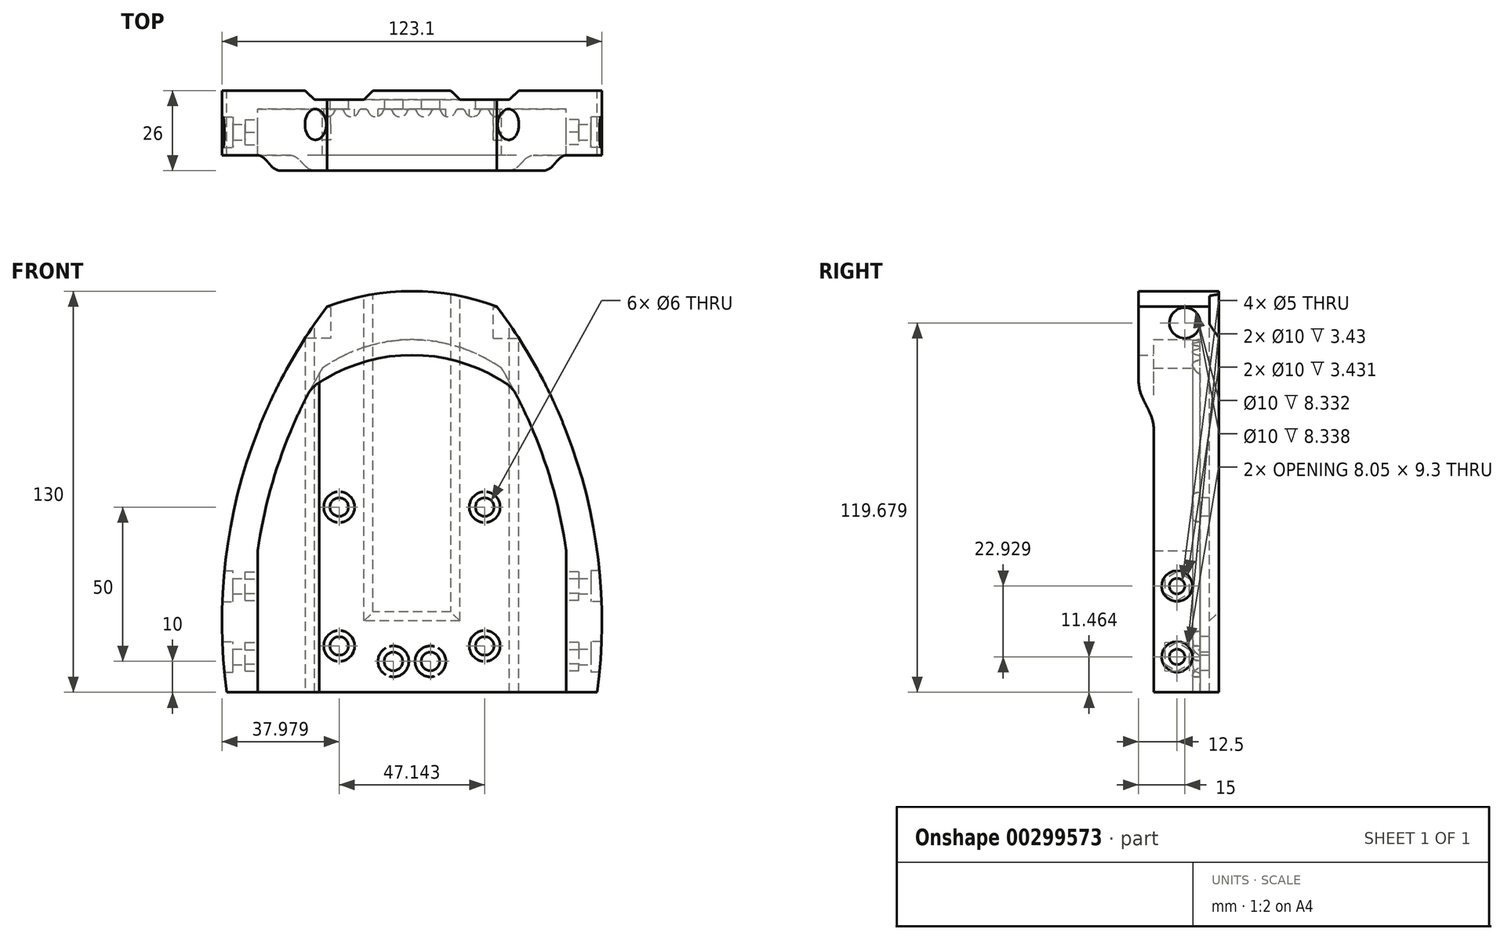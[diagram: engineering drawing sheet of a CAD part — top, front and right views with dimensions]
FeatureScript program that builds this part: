
annotation { "Feature Type Name" : "Feature", "Feature Type Description" : "" }
export const myFeature = defineFeature(function(context is Context, id is Id, definition is map)
    precondition{}
    {
        {
            assignVariable(context, id + "F0", {"name" : "TWall", "anyValue" : 10});
        }
        {
            var Q0;
            Q0=qCreatedBy(makeId("Front.planeOp"),FACE);
            var sketch = newSketch(context, id + "F1", { "sketchPlane" : qUnion([Q0])});
            skArc(sketch, "E0", {"start": v(-27.5, 125) * mm, "mid": v(-56.08, 65.7) * mm, "end": v(-60, 0) * mm});
            skArc(sketch, "E1", {"start": v(0, 130) * mm, "mid": v(-13.98, 128.74) * mm, "end": v(-27.5, 125) * mm});
            skLineSegment(sketch, "E2", {"start": v(-60, 0) * mm, "end": v(0, 0) * mm});
            skArc(sketch, "E3.MirrorCS", {"start": v(0, 130) * mm, "mid": v(13.98, 128.74) * mm, "end": v(27.5, 125) * mm});
            skArc(sketch, "E4.MirrorCS", {"start": v(27.5, 125) * mm, "mid": v(56.08, 65.7) * mm, "end": v(60, 0) * mm});
            skLineSegment(sketch, "E5.MirrorCS", {"start": v(60, 0) * mm, "end": v(0, 0) * mm});
            skSolve(sketch);
        }
        {
            var Q0;
            Q0 = qSketchRegion(id + "F1", true);
            extrude(context, id + "F2", {"entities" : qUnion([Q0]), "depth" : 3 * mm});
        }
        {
            var Q0;
            Q0=makeQuery(id+"F2.opExtrude","CAP_FACE",FACE,{"disambiguationData":[OSD([sQuery(id+"F1.wireOp",EDGE,"E0"),sQuery(id+"F1.wireOp",EDGE,"E1"),sQuery(id+"F1.wireOp",EDGE,"E2"),sQuery(id+"F1.wireOp",EDGE,"E3.MirrorCS"),sQuery(id+"F1.wireOp",EDGE,"E4.MirrorCS"),sQuery(id+"F1.wireOp",EDGE,"E5.MirrorCS")])],"isStart":false});
            var sketch = newSketch(context, id + "F3", { "sketchPlane" : qUnion([Q0])});
            skArc(sketch, "E6", {"start": v(27.5, 125) * mm, "mid": v(0, 130) * mm, "end": v(-27.5, 125) * mm});
            skArc(sketch, "E7", {"start": v(-27.5, 125) * mm, "mid": v(-56.08, 65.7) * mm, "end": v(-60, 0) * mm});
            skArc(sketch, "E8", {"start": v(60, 0) * mm, "mid": v(56.08, 65.7) * mm, "end": v(27.5, 125) * mm});
            skArc(sketch, "E9", {"start": v(29.01, 105) * mm, "mid": v(0, 114.28) * mm, "end": v(-29.01, 105) * mm});
            skArc(sketch, "E10", {"start": v(-29.01, 105) * mm, "mid": v(-48.55, 54.3) * mm, "end": v(-50, 0) * mm});
            skArc(sketch, "E11", {"start": v(50, 0) * mm, "mid": v(48.55, 54.3) * mm, "end": v(29.01, 105) * mm});
            skLineSegment(sketch, "E12", {"start": v(-60, 0) * mm, "end": v(-50, 0) * mm});
            skLineSegment(sketch, "E13", {"start": v(50, 0) * mm, "end": v(60, 0) * mm});
            skLineSegment(sketch, "E14", {"start": v(-50, 45.86) * mm, "end": v(-50, 0) * mm});
            skPoint(sketch, "E15", {"position": v(-50, 43.93) * mm});
            skLineSegment(sketch, "E16.MirrorCS", {"start": v(50, 45.86) * mm, "end": v(50, 0) * mm});
            skSolve(sketch);
        }
        {
            var Q0;
            Q0 = qSketchRegion(id + "F3", true);
            extrude(context, id + "F4", {"entities" : qUnion([Q0]), "operationType" : NewBodyOperationType.ADD, "depth" : 15 * mm});
        }
        {
            var Q0;
            Q0=makeQuery(id+"F2.opExtrude","SWEPT_FACE",FACE,{"disambiguationData":[OSD([sQuery(id+"F1.wireOp",EDGE,"E2"),sQuery(id+"F1.wireOp",EDGE,"E5.MirrorCS")])]});
            var sketch = newSketch(context, id + "F5", { "sketchPlane" : qUnion([Q0])});
            skArc(sketch, "E17", {"start": v(-25, 3) * mm, "mid": v(-27.5, 5.5) * mm, "end": v(-30, 3) * mm});
            skLineSegment(sketch, "E18", {"start": v(-30, 3) * mm, "end": v(-25, 3) * mm});
            skArc(sketch, "E19.1.0.0", {"start": v(-17.14, 3) * mm, "mid": v(-19.64, 5.5) * mm, "end": v(-22.14, 3) * mm});
            skLineSegment(sketch, "E19.1.0.1", {"start": v(-22.14, 3) * mm, "end": v(-17.14, 3) * mm});
            skArc(sketch, "E19.2.0.0", {"start": v(-9.29, 3) * mm, "mid": v(-11.79, 5.5) * mm, "end": v(-14.29, 3) * mm});
            skLineSegment(sketch, "E19.2.0.1", {"start": v(-14.29, 3) * mm, "end": v(-9.29, 3) * mm});
            skArc(sketch, "E19.3.0.0", {"start": v(-1.43, 3) * mm, "mid": v(-3.93, 5.5) * mm, "end": v(-6.43, 3) * mm});
            skLineSegment(sketch, "E19.3.0.1", {"start": v(-6.43, 3) * mm, "end": v(-1.43, 3) * mm});
            skArc(sketch, "E19.4.0.0", {"start": v(6.43, 3) * mm, "mid": v(3.93, 5.5) * mm, "end": v(1.43, 3) * mm});
            skLineSegment(sketch, "E19.4.0.1", {"start": v(1.43, 3) * mm, "end": v(6.43, 3) * mm});
            skArc(sketch, "E19.5.0.0", {"start": v(14.29, 3) * mm, "mid": v(11.79, 5.5) * mm, "end": v(9.29, 3) * mm});
            skLineSegment(sketch, "E19.5.0.1", {"start": v(9.29, 3) * mm, "end": v(14.29, 3) * mm});
            skArc(sketch, "E19.6.0.0", {"start": v(22.14, 3) * mm, "mid": v(19.64, 5.5) * mm, "end": v(17.14, 3) * mm});
            skLineSegment(sketch, "E19.6.0.1", {"start": v(17.14, 3) * mm, "end": v(22.14, 3) * mm});
            skArc(sketch, "E19.7.0.0", {"start": v(30, 3) * mm, "mid": v(27.5, 5.5) * mm, "end": v(25, 3) * mm});
            skLineSegment(sketch, "E19.7.0.1", {"start": v(25, 3) * mm, "end": v(30, 3) * mm});
            skLineSegment(sketch, "E19.direction1", {"start": v(-30, 3) * mm, "end": v(-22.14, 3) * mm, "construction": true});
            skSolve(sketch);
        }
        {
            var Q0;
            Q0 = qSketchRegion(id + "F5", true);
            extrude(context, id + "F6", {"entities" : qUnion([Q0]), "operationType" : NewBodyOperationType.ADD, "endBound" : BoundingType.UP_TO_NEXT, "oppositeDirection" : true, "depth" : 25 * mm});
        }
        {
            var Q0;
            {var subQ0=sQuery(id+"F5.wireOp",EDGE,"E18");var subQ1=sQuery(id+"F5.wireOp",EDGE,"E17");var subQ2=sQuery(id+"F1.wireOp",EDGE,"E5.MirrorCS");var subQ3=sQuery(id+"F1.wireOp",EDGE,"E2");Q0=makeQuery(id+"F6.opExtrude","SWEPT_EDGE",EDGE,{"disambiguationData":[OSD([subQ3,subQ2,subQ1,subQ0]),TDD([makeQuery(id+"F5.imprint","INTERSECT",VERTEX,{"disambiguationData":[OD(1.0)],"derivedFrom":[makeQuery(id+"F2.opExtrude","CAP_EDGE",EDGE,{"disambiguationData":[OSD([subQ3,subQ2])],"isStart":false}),subQ1,subQ0]})])]});}
            var Q1;
            {var subQ0=sQuery(id+"F5.wireOp",EDGE,"E18");var subQ1=sQuery(id+"F5.wireOp",EDGE,"E17");var subQ2=sQuery(id+"F1.wireOp",EDGE,"E5.MirrorCS");var subQ3=sQuery(id+"F1.wireOp",EDGE,"E2");Q1=makeQuery(id+"F6.opExtrude","SWEPT_EDGE",EDGE,{"disambiguationData":[OSD([subQ3,subQ2,subQ1,subQ0]),TDD([makeQuery(id+"F5.imprint","INTERSECT",VERTEX,{"disambiguationData":[OD(0.0)],"derivedFrom":[makeQuery(id+"F2.opExtrude","CAP_EDGE",EDGE,{"disambiguationData":[OSD([subQ3,subQ2])],"isStart":false}),subQ1,subQ0]})])]});}
            var Q2;
            {var subQ0=sQuery(id+"F5.wireOp",EDGE,"E19.1.0.1");var subQ1=sQuery(id+"F5.wireOp",EDGE,"E19.1.0.0");var subQ2=sQuery(id+"F1.wireOp",EDGE,"E5.MirrorCS");var subQ3=sQuery(id+"F1.wireOp",EDGE,"E2");Q2=makeQuery(id+"F6.opExtrude","SWEPT_EDGE",EDGE,{"disambiguationData":[OSD([subQ3,subQ2,subQ1,subQ0]),TDD([makeQuery(id+"F5.imprint","INTERSECT",VERTEX,{"disambiguationData":[OD(0.0)],"derivedFrom":[makeQuery(id+"F2.opExtrude","CAP_EDGE",EDGE,{"disambiguationData":[OSD([subQ3,subQ2])],"isStart":false}),subQ1,subQ0]})])]});}
            var Q3;
            {var subQ0=sQuery(id+"F5.wireOp",EDGE,"E19.2.0.1");var subQ1=sQuery(id+"F5.wireOp",EDGE,"E19.2.0.0");var subQ2=sQuery(id+"F1.wireOp",EDGE,"E5.MirrorCS");var subQ3=sQuery(id+"F1.wireOp",EDGE,"E2");Q3=makeQuery(id+"F6.opExtrude","SWEPT_EDGE",EDGE,{"disambiguationData":[OSD([subQ3,subQ2,subQ1,subQ0]),TDD([makeQuery(id+"F5.imprint","INTERSECT",VERTEX,{"disambiguationData":[OD(0.0)],"derivedFrom":[makeQuery(id+"F2.opExtrude","CAP_EDGE",EDGE,{"disambiguationData":[OSD([subQ3,subQ2])],"isStart":false}),subQ1,subQ0]})])]});}
            var Q4;
            {var subQ0=sQuery(id+"F5.wireOp",EDGE,"E19.3.0.1");var subQ1=sQuery(id+"F5.wireOp",EDGE,"E19.3.0.0");var subQ2=sQuery(id+"F1.wireOp",EDGE,"E5.MirrorCS");var subQ3=sQuery(id+"F1.wireOp",EDGE,"E2");Q4=makeQuery(id+"F6.opExtrude","SWEPT_EDGE",EDGE,{"disambiguationData":[OSD([subQ3,subQ2,subQ1,subQ0]),TDD([makeQuery(id+"F5.imprint","INTERSECT",VERTEX,{"disambiguationData":[OD(0.0)],"derivedFrom":[makeQuery(id+"F2.opExtrude","CAP_EDGE",EDGE,{"disambiguationData":[OSD([subQ3,subQ2])],"isStart":false}),subQ1,subQ0]})])]});}
            var Q5;
            {var subQ0=sQuery(id+"F5.wireOp",EDGE,"E19.4.0.1");var subQ1=sQuery(id+"F5.wireOp",EDGE,"E19.4.0.0");var subQ2=sQuery(id+"F1.wireOp",EDGE,"E5.MirrorCS");var subQ3=sQuery(id+"F1.wireOp",EDGE,"E2");Q5=makeQuery(id+"F6.opExtrude","SWEPT_EDGE",EDGE,{"disambiguationData":[OSD([subQ3,subQ2,subQ1,subQ0]),TDD([makeQuery(id+"F5.imprint","INTERSECT",VERTEX,{"disambiguationData":[OD(0.0)],"derivedFrom":[makeQuery(id+"F2.opExtrude","CAP_EDGE",EDGE,{"disambiguationData":[OSD([subQ3,subQ2])],"isStart":false}),subQ1,subQ0]})])]});}
            var Q6;
            {var subQ0=sQuery(id+"F5.wireOp",EDGE,"E19.5.0.1");var subQ1=sQuery(id+"F5.wireOp",EDGE,"E19.5.0.0");var subQ2=sQuery(id+"F1.wireOp",EDGE,"E5.MirrorCS");var subQ3=sQuery(id+"F1.wireOp",EDGE,"E2");Q6=makeQuery(id+"F6.opExtrude","SWEPT_EDGE",EDGE,{"disambiguationData":[OSD([subQ3,subQ2,subQ1,subQ0]),TDD([makeQuery(id+"F5.imprint","INTERSECT",VERTEX,{"disambiguationData":[OD(0.0)],"derivedFrom":[makeQuery(id+"F2.opExtrude","CAP_EDGE",EDGE,{"disambiguationData":[OSD([subQ3,subQ2])],"isStart":false}),subQ1,subQ0]})])]});}
            var Q7;
            {var subQ0=sQuery(id+"F5.wireOp",EDGE,"E19.6.0.1");var subQ1=sQuery(id+"F5.wireOp",EDGE,"E19.6.0.0");var subQ2=sQuery(id+"F1.wireOp",EDGE,"E5.MirrorCS");var subQ3=sQuery(id+"F1.wireOp",EDGE,"E2");Q7=makeQuery(id+"F6.opExtrude","SWEPT_EDGE",EDGE,{"disambiguationData":[OSD([subQ3,subQ2,subQ1,subQ0]),TDD([makeQuery(id+"F5.imprint","INTERSECT",VERTEX,{"disambiguationData":[OD(0.0)],"derivedFrom":[makeQuery(id+"F2.opExtrude","CAP_EDGE",EDGE,{"disambiguationData":[OSD([subQ3,subQ2])],"isStart":false}),subQ1,subQ0]})])]});}
            var Q8;
            {var subQ0=sQuery(id+"F5.wireOp",EDGE,"E19.7.0.1");var subQ1=sQuery(id+"F5.wireOp",EDGE,"E19.7.0.0");var subQ2=sQuery(id+"F1.wireOp",EDGE,"E5.MirrorCS");var subQ3=sQuery(id+"F1.wireOp",EDGE,"E2");Q8=makeQuery(id+"F6.opExtrude","SWEPT_EDGE",EDGE,{"disambiguationData":[OSD([subQ3,subQ2,subQ1,subQ0]),TDD([makeQuery(id+"F5.imprint","INTERSECT",VERTEX,{"disambiguationData":[OD(0.0)],"derivedFrom":[makeQuery(id+"F2.opExtrude","CAP_EDGE",EDGE,{"disambiguationData":[OSD([subQ3,subQ2])],"isStart":false}),subQ1,subQ0]})])]});}
            var Q9;
            {var subQ0=sQuery(id+"F5.wireOp",EDGE,"E19.8.0.1");var subQ1=sQuery(id+"F5.wireOp",EDGE,"E19.8.0.0");var subQ2=sQuery(id+"F1.wireOp",EDGE,"E5.MirrorCS");var subQ3=sQuery(id+"F1.wireOp",EDGE,"E2");Q9=makeQuery(id+"F6.opExtrude","SWEPT_EDGE",EDGE,{"disambiguationData":[OSD([subQ3,subQ2,subQ1,subQ0]),TDD([makeQuery(id+"F5.imprint","INTERSECT",VERTEX,{"disambiguationData":[OD(0.0)],"derivedFrom":[makeQuery(id+"F2.opExtrude","CAP_EDGE",EDGE,{"disambiguationData":[OSD([subQ3,subQ2])],"isStart":false}),subQ1,subQ0]})])]});}
            var Q10;
            {var subQ0=sQuery(id+"F5.wireOp",EDGE,"E19.9.0.1");var subQ1=sQuery(id+"F5.wireOp",EDGE,"E19.9.0.0");var subQ2=sQuery(id+"F1.wireOp",EDGE,"E5.MirrorCS");var subQ3=sQuery(id+"F1.wireOp",EDGE,"E2");Q10=makeQuery(id+"F6.opExtrude","SWEPT_EDGE",EDGE,{"disambiguationData":[OSD([subQ3,subQ2,subQ1,subQ0]),TDD([makeQuery(id+"F5.imprint","INTERSECT",VERTEX,{"disambiguationData":[OD(0.0)],"derivedFrom":[makeQuery(id+"F2.opExtrude","CAP_EDGE",EDGE,{"disambiguationData":[OSD([subQ3,subQ2])],"isStart":false}),subQ1,subQ0]})])]});}
            var Q11;
            {var subQ0=sQuery(id+"F5.wireOp",EDGE,"E19.1.0.1");var subQ1=sQuery(id+"F5.wireOp",EDGE,"E19.1.0.0");var subQ2=sQuery(id+"F1.wireOp",EDGE,"E5.MirrorCS");var subQ3=sQuery(id+"F1.wireOp",EDGE,"E2");Q11=makeQuery(id+"F6.opExtrude","SWEPT_EDGE",EDGE,{"disambiguationData":[OSD([subQ3,subQ2,subQ1,subQ0]),TDD([makeQuery(id+"F5.imprint","INTERSECT",VERTEX,{"disambiguationData":[OD(1.0)],"derivedFrom":[makeQuery(id+"F2.opExtrude","CAP_EDGE",EDGE,{"disambiguationData":[OSD([subQ3,subQ2])],"isStart":false}),subQ1,subQ0]})])]});}
            var Q12;
            {var subQ0=sQuery(id+"F5.wireOp",EDGE,"E19.2.0.1");var subQ1=sQuery(id+"F5.wireOp",EDGE,"E19.2.0.0");var subQ2=sQuery(id+"F1.wireOp",EDGE,"E5.MirrorCS");var subQ3=sQuery(id+"F1.wireOp",EDGE,"E2");Q12=makeQuery(id+"F6.opExtrude","SWEPT_EDGE",EDGE,{"disambiguationData":[OSD([subQ3,subQ2,subQ1,subQ0]),TDD([makeQuery(id+"F5.imprint","INTERSECT",VERTEX,{"disambiguationData":[OD(1.0)],"derivedFrom":[makeQuery(id+"F2.opExtrude","CAP_EDGE",EDGE,{"disambiguationData":[OSD([subQ3,subQ2])],"isStart":false}),subQ1,subQ0]})])]});}
            var Q13;
            {var subQ0=sQuery(id+"F5.wireOp",EDGE,"E19.3.0.1");var subQ1=sQuery(id+"F5.wireOp",EDGE,"E19.3.0.0");var subQ2=sQuery(id+"F1.wireOp",EDGE,"E5.MirrorCS");var subQ3=sQuery(id+"F1.wireOp",EDGE,"E2");Q13=makeQuery(id+"F6.opExtrude","SWEPT_EDGE",EDGE,{"disambiguationData":[OSD([subQ3,subQ2,subQ1,subQ0]),TDD([makeQuery(id+"F5.imprint","INTERSECT",VERTEX,{"disambiguationData":[OD(1.0)],"derivedFrom":[makeQuery(id+"F2.opExtrude","CAP_EDGE",EDGE,{"disambiguationData":[OSD([subQ3,subQ2])],"isStart":false}),subQ1,subQ0]})])]});}
            var Q14;
            {var subQ0=sQuery(id+"F5.wireOp",EDGE,"E19.4.0.1");var subQ1=sQuery(id+"F5.wireOp",EDGE,"E19.4.0.0");var subQ2=sQuery(id+"F1.wireOp",EDGE,"E5.MirrorCS");var subQ3=sQuery(id+"F1.wireOp",EDGE,"E2");Q14=makeQuery(id+"F6.opExtrude","SWEPT_EDGE",EDGE,{"disambiguationData":[OSD([subQ3,subQ2,subQ1,subQ0]),TDD([makeQuery(id+"F5.imprint","INTERSECT",VERTEX,{"disambiguationData":[OD(1.0)],"derivedFrom":[makeQuery(id+"F2.opExtrude","CAP_EDGE",EDGE,{"disambiguationData":[OSD([subQ3,subQ2])],"isStart":false}),subQ1,subQ0]})])]});}
            var Q15;
            {var subQ0=sQuery(id+"F5.wireOp",EDGE,"E19.5.0.1");var subQ1=sQuery(id+"F5.wireOp",EDGE,"E19.5.0.0");var subQ2=sQuery(id+"F1.wireOp",EDGE,"E5.MirrorCS");var subQ3=sQuery(id+"F1.wireOp",EDGE,"E2");Q15=makeQuery(id+"F6.opExtrude","SWEPT_EDGE",EDGE,{"disambiguationData":[OSD([subQ3,subQ2,subQ1,subQ0]),TDD([makeQuery(id+"F5.imprint","INTERSECT",VERTEX,{"disambiguationData":[OD(1.0)],"derivedFrom":[makeQuery(id+"F2.opExtrude","CAP_EDGE",EDGE,{"disambiguationData":[OSD([subQ3,subQ2])],"isStart":false}),subQ1,subQ0]})])]});}
            var Q16;
            {var subQ0=sQuery(id+"F5.wireOp",EDGE,"E19.6.0.1");var subQ1=sQuery(id+"F5.wireOp",EDGE,"E19.6.0.0");var subQ2=sQuery(id+"F1.wireOp",EDGE,"E5.MirrorCS");var subQ3=sQuery(id+"F1.wireOp",EDGE,"E2");Q16=makeQuery(id+"F6.opExtrude","SWEPT_EDGE",EDGE,{"disambiguationData":[OSD([subQ3,subQ2,subQ1,subQ0]),TDD([makeQuery(id+"F5.imprint","INTERSECT",VERTEX,{"disambiguationData":[OD(1.0)],"derivedFrom":[makeQuery(id+"F2.opExtrude","CAP_EDGE",EDGE,{"disambiguationData":[OSD([subQ3,subQ2])],"isStart":false}),subQ1,subQ0]})])]});}
            var Q17;
            {var subQ0=sQuery(id+"F5.wireOp",EDGE,"E19.7.0.1");var subQ1=sQuery(id+"F5.wireOp",EDGE,"E19.7.0.0");var subQ2=sQuery(id+"F1.wireOp",EDGE,"E5.MirrorCS");var subQ3=sQuery(id+"F1.wireOp",EDGE,"E2");Q17=makeQuery(id+"F6.opExtrude","SWEPT_EDGE",EDGE,{"disambiguationData":[OSD([subQ3,subQ2,subQ1,subQ0]),TDD([makeQuery(id+"F5.imprint","INTERSECT",VERTEX,{"disambiguationData":[OD(1.0)],"derivedFrom":[makeQuery(id+"F2.opExtrude","CAP_EDGE",EDGE,{"disambiguationData":[OSD([subQ3,subQ2])],"isStart":false}),subQ1,subQ0]})])]});}
            var Q18;
            {var subQ0=sQuery(id+"F5.wireOp",EDGE,"E19.8.0.1");var subQ1=sQuery(id+"F5.wireOp",EDGE,"E19.8.0.0");var subQ2=sQuery(id+"F1.wireOp",EDGE,"E5.MirrorCS");var subQ3=sQuery(id+"F1.wireOp",EDGE,"E2");Q18=makeQuery(id+"F6.opExtrude","SWEPT_EDGE",EDGE,{"disambiguationData":[OSD([subQ3,subQ2,subQ1,subQ0]),TDD([makeQuery(id+"F5.imprint","INTERSECT",VERTEX,{"disambiguationData":[OD(1.0)],"derivedFrom":[makeQuery(id+"F2.opExtrude","CAP_EDGE",EDGE,{"disambiguationData":[OSD([subQ3,subQ2])],"isStart":false}),subQ1,subQ0]})])]});}
            var Q19;
            {var subQ0=sQuery(id+"F5.wireOp",EDGE,"E19.9.0.1");var subQ1=sQuery(id+"F5.wireOp",EDGE,"E19.9.0.0");var subQ2=sQuery(id+"F1.wireOp",EDGE,"E5.MirrorCS");var subQ3=sQuery(id+"F1.wireOp",EDGE,"E2");Q19=makeQuery(id+"F6.opExtrude","SWEPT_EDGE",EDGE,{"disambiguationData":[OSD([subQ3,subQ2,subQ1,subQ0]),TDD([makeQuery(id+"F5.imprint","INTERSECT",VERTEX,{"disambiguationData":[OD(1.0)],"derivedFrom":[makeQuery(id+"F2.opExtrude","CAP_EDGE",EDGE,{"disambiguationData":[OSD([subQ3,subQ2])],"isStart":false}),subQ1,subQ0]})])]});}
            fillet(context, id + "F7", {"entities" : qUnion([Q0, Q1, Q2, Q3, Q4, Q5, Q6, Q7, Q8, Q9, Q10, Q11, Q12, Q13, Q14, Q15, Q16, Q17, Q18, Q19]), "radius" : 1 * mm, "tangentPropagation" : true, "allowEdgeOverflow" : false});
        }
        {
            var Q0;
            Q0=makeQuery(id+"F4.opExtrude","CAP_FACE",FACE,{"disambiguationData":[OSD([sQuery(id+"F3.wireOp",EDGE,"E6"),sQuery(id+"F3.wireOp",EDGE,"E7"),sQuery(id+"F3.wireOp",EDGE,"E8"),sQuery(id+"F3.wireOp",EDGE,"E9"),sQuery(id+"F3.wireOp",EDGE,"E10"),sQuery(id+"F3.wireOp",EDGE,"E11"),sQuery(id+"F3.wireOp",EDGE,"E12"),sQuery(id+"F3.wireOp",EDGE,"E13")])],"isStart":false});
            var sketch = newSketch(context, id + "F8", { "sketchPlane" : qUnion([Q0])});
            skPoint(sketch, "E20", {"position": v(-31.34, 119.68) * mm});
            skPoint(sketch, "E21", {"position": v(31.34, 119.68) * mm});
            skSolve(sketch);
        }
        {
            var Q0;
            Q0=qCreatedBy(makeId("Right.planeOp"),FACE);
            cPlane(context, id + "F9", {"entities" : qUnion([Q0]), "cplaneType" : CPlaneType.OFFSET, "offset" : (62.67 / 2) * mm, "width" : 150 * mm, "height" : 150 * mm});
        }
        {
            var Q0;
            Q0=qCreatedBy(makeId("Right.planeOp"),FACE);
            cPlane(context, id + "F10", {"entities" : qUnion([Q0]), "cplaneType" : CPlaneType.OFFSET, "offset" : (62.67 / 2) * mm, "oppositeDirection" : true, "width" : 150 * mm, "height" : 150 * mm});
        }
        {
            var Q0;
            Q0=qCreatedBy(id+"F9.planeOp",FACE);
            var sketch = newSketch(context, id + "F11", { "sketchPlane" : qUnion([Q0])});
            skCircle(sketch, "E22", {"center": v(-8, 119.68) * mm, "radius": 5 * mm});
            skSolve(sketch);
        }
        {
            var Q0;
            Q0 = qSketchRegion(id + "F11", true);
            extrude(context, id + "F12", {"entities" : qUnion([Q0]), "operationType" : NewBodyOperationType.REMOVE, "oppositeDirection" : true, "depth" : 5 * mm, "hasSecondDirection" : true, "secondDirectionOppositeDirection" : false, "secondDirectionDepth" : 25 * mm});
        }
        {
            var Q0;
            Q0=qCreatedBy(id+"F10.planeOp",FACE);
            var sketch = newSketch(context, id + "F13", { "sketchPlane" : qUnion([Q0])});
            skCircle(sketch, "E23", {"center": v(-8, 119.68) * mm, "radius": 5 * mm});
            skSolve(sketch);
        }
        {
            var Q0;
            Q0 = qSketchRegion(id + "F13", true);
            extrude(context, id + "F14", {"entities" : qUnion([Q0]), "operationType" : NewBodyOperationType.REMOVE, "depth" : 5 * mm, "hasSecondDirection" : true, "secondDirectionOppositeDirection" : true, "secondDirectionDepth" : 25 * mm});
        }
        {
            var Q0;
            {var subQ0=makeQuery(id+"F6.opExtrude","CAP_FACE",FACE,{"disambiguationData":[OSD([sQuery(id+"F5.wireOp",EDGE,"E19.5.0.0"),sQuery(id+"F5.wireOp",EDGE,"E19.5.0.1")])],"isStart":true});var subQ1=sQuery(id+"F1.wireOp",EDGE,"E5.MirrorCS");var subQ2=sQuery(id+"F1.wireOp",EDGE,"E2");var subQ3=makeQuery(id+"F2.opExtrude","SWEPT_FACE",FACE,{"disambiguationData":[OSD([subQ2,subQ1])]});var subQ4=sQuery(id+"F5.wireOp",EDGE,"E19.3.0.0");var subQ5=makeQuery(id+"F6.opExtrude","CAP_FACE",FACE,{"disambiguationData":[OSD([subQ4,sQuery(id+"F5.wireOp",EDGE,"E19.3.0.1")])],"isStart":true});var subQ6=sQuery(id+"F5.wireOp",EDGE,"E19.2.0.0");var subQ7=makeQuery(id+"F6.opExtrude","CAP_FACE",FACE,{"disambiguationData":[OSD([subQ6,sQuery(id+"F5.wireOp",EDGE,"E19.2.0.1")])],"isStart":true});var subQ8=makeQuery(id+"F6.opExtrude","SWEPT_FACE",FACE,{"disambiguationData":[OSD([subQ6])]});var subQ9=sQuery(id+"F5.wireOp",EDGE,"E19.1.0.0");var subQ10=makeQuery(id+"F6.opExtrude","CAP_FACE",FACE,{"disambiguationData":[OSD([subQ9,sQuery(id+"F5.wireOp",EDGE,"E19.1.0.1")])],"isStart":true});var subQ11=makeQuery(id+"F6.opExtrude","CAP_FACE",FACE,{"disambiguationData":[OSD([sQuery(id+"F5.wireOp",EDGE,"E19.4.0.0"),sQuery(id+"F5.wireOp",EDGE,"E19.4.0.1")])],"isStart":true});var subQ12=makeQuery(id+"F4.opExtrude","SWEPT_FACE",FACE,{"disambiguationData":[OSD([sQuery(id+"F3.wireOp",EDGE,"E9")])]});var subQ13=sQuery(id+"F5.wireOp",EDGE,"E17");var subQ14=makeQuery(id+"F6.opExtrude","CAP_FACE",FACE,{"disambiguationData":[OSD([subQ13,sQuery(id+"F5.wireOp",EDGE,"E18")])],"isStart":true});var subQ15=makeQuery(id+"F6.opExtrude","CAP_FACE",FACE,{"disambiguationData":[OSD([sQuery(id+"F5.wireOp",EDGE,"E19.6.0.0"),sQuery(id+"F5.wireOp",EDGE,"E19.6.0.1")])],"isStart":true});var subQ16=makeQuery(id+"F6.opExtrude","CAP_FACE",FACE,{"disambiguationData":[OSD([sQuery(id+"F5.wireOp",EDGE,"E19.7.0.0"),sQuery(id+"F5.wireOp",EDGE,"E19.7.0.1")])],"isStart":true});var subQ17=makeQuery(id+"F6.opExtrude","CAP_FACE",FACE,{"disambiguationData":[OSD([sQuery(id+"F5.wireOp",EDGE,"E19.8.0.0"),sQuery(id+"F5.wireOp",EDGE,"E19.8.0.1")])],"isStart":true});var subQ18=makeQuery(id+"F6.opExtrude","CAP_FACE",FACE,{"disambiguationData":[OSD([sQuery(id+"F5.wireOp",EDGE,"E19.9.0.0"),sQuery(id+"F5.wireOp",EDGE,"E19.9.0.1")])],"isStart":true});var subQ19=makeQuery(id+"F2.opExtrude","CAP_FACE",FACE,{"disambiguationData":[OSD([sQuery(id+"F1.wireOp",EDGE,"E0"),sQuery(id+"F1.wireOp",EDGE,"E1"),subQ2,sQuery(id+"F1.wireOp",EDGE,"E3.MirrorCS"),sQuery(id+"F1.wireOp",EDGE,"E4.MirrorCS"),subQ1])],"isStart":false});var subQ20=makeQuery(id+"F6.opExtrude","SWEPT_FACE",FACE,{"disambiguationData":[OSD([subQ9])]});Q0=makeQuery(id+"FagDk5R1PXxC9WP_1.boolean.opBoolean","MERGE",FACE,{"derivedFrom":[makeQuery(id+"F6.boolean.opBoolean","SPLIT",FACE,{"disambiguationData":[TD([subQ3,subQ12,makeQuery(id+"F6.opExtrude","SWEPT_FACE",FACE,{"disambiguationData":[OSD([subQ13])]}),subQ14,subQ20,subQ10,subQ7,subQ5,subQ11,subQ0,subQ15,subQ16,subQ17,subQ18])],"derivedFrom":subQ19}),makeQuery(id+"F6.boolean.opBoolean","SPLIT",FACE,{"disambiguationData":[TD([subQ3,subQ12,subQ14,subQ20,subQ10,subQ8,subQ7,subQ5,subQ11,subQ0,subQ15,subQ16,subQ17,subQ18])],"derivedFrom":subQ19}),makeQuery(id+"F6.boolean.opBoolean","SPLIT",FACE,{"disambiguationData":[TD([subQ3,subQ12,subQ14,subQ10,subQ8,subQ7,makeQuery(id+"F6.opExtrude","SWEPT_FACE",FACE,{"disambiguationData":[OSD([subQ4])]}),subQ5,subQ11,subQ0,subQ15,subQ16,subQ17,subQ18])],"derivedFrom":subQ19}),makeQuery(id+"FagDk5R1PXxC9WP_1.opExtrude","SWEPT_FACE",FACE,{"disambiguationData":[OSD([sQuery(id+"FtMZI0YXXD80vIJ_1.wireOp",EDGE,"6BlepP5m-DG3n-HtGD-IaAT-YB7duayLEJRe.bottom")])]})]});}
            var sketch = newSketch(context, id + "F15", { "sketchPlane" : qUnion([Q0])});
            skCircle(sketch, "E24", {"center": v(-23.57, 15) * mm, "radius": 3 * mm});
            skPoint(sketch, "E24.centerSnap0", {"position": v(-23.57, 0) * mm});
            skCircle(sketch, "E25", {"center": v(-23.57, 60) * mm, "radius": 3 * mm});
            skCircle(sketch, "E26.MirrorC", {"center": v(23.57, 15) * mm, "radius": 3 * mm});
            skCircle(sketch, "E27.MirrorC", {"center": v(23.57, 60) * mm, "radius": 3 * mm});
            skPoint(sketch, "E28", {"position": v(0, 0) * mm});
            skCircle(sketch, "E29", {"center": v(6, 10) * mm, "radius": 3 * mm});
            skCircle(sketch, "E30", {"center": v(-6, 10) * mm, "radius": 3 * mm});
            skSolve(sketch);
        }
        {
            var Q0;
            Q0 = qSketchRegion(id + "F15", true);
            extrude(context, id + "F16", {"entities" : qUnion([Q0]), "operationType" : NewBodyOperationType.REMOVE, "oppositeDirection" : true, "depth" : 25 * mm});
        }
        {
            var Q0;
            {var subQ0=sQuery(id+"F5.wireOp",EDGE,"E17");var subQ1=makeQuery(id+"F4.opExtrude","SWEPT_FACE",FACE,{"disambiguationData":[OSD([sQuery(id+"F3.wireOp",EDGE,"E10")])]});var subQ2=makeQuery(id+"F4.opExtrude","SWEPT_FACE",FACE,{"disambiguationData":[OSD([sQuery(id+"F3.wireOp",EDGE,"E7")])]});var subQ3=sQuery(id+"F1.wireOp",EDGE,"E5.MirrorCS");var subQ4=sQuery(id+"F1.wireOp",EDGE,"E2");var subQ5=sQuery(id+"F1.wireOp",EDGE,"E0");var subQ6=makeQuery(id+"F2.opExtrude","CAP_FACE",FACE,{"disambiguationData":[OSD([subQ5,sQuery(id+"F1.wireOp",EDGE,"E1"),subQ4,sQuery(id+"F1.wireOp",EDGE,"E3.MirrorCS"),sQuery(id+"F1.wireOp",EDGE,"E4.MirrorCS"),subQ3])],"isStart":false});var subQ7=makeQuery(id+"F2.opExtrude","SWEPT_FACE",FACE,{"disambiguationData":[OSD([subQ5])]});Q0=makeQuery(id+"F6.boolean.opBoolean","SPLIT",FACE,{"disambiguationData":[TD([subQ7,makeQuery(id+"F2.opExtrude","SWEPT_FACE",FACE,{"disambiguationData":[OSD([subQ4,subQ3])]}),subQ2,subQ1,makeQuery(id+"FEmyDYQQVgRQXe1_1.boolean.opBoolean","COPY",FACE,{"disambiguationData":[TD([subQ7])],"derivedFrom":makeQuery(id+"FEmyDYQQVgRQXe1_1.opExtrude","SWEPT_FACE",FACE,{"disambiguationData":[OSD([sQuery(id+"F95mhF6FaMZOlkV_1.wireOp",EDGE,"16wo293t-KL3b-4ck3-VDR1-H0NEiYk0Jyv5")])]})}),makeQuery(id+"F6.opExtrude","SWEPT_FACE",FACE,{"disambiguationData":[OSD([subQ0])]}),makeQuery(id+"F6.opExtrude","CAP_FACE",FACE,{"disambiguationData":[OSD([subQ0,sQuery(id+"F5.wireOp",EDGE,"E18")])],"isStart":true}),makeQuery(id+"F6.opExtrude","CAP_FACE",FACE,{"disambiguationData":[OSD([sQuery(id+"F5.wireOp",EDGE,"E19.1.0.0"),sQuery(id+"F5.wireOp",EDGE,"E19.1.0.1")])],"isStart":true}),makeQuery(id+"F6.opExtrude","CAP_FACE",FACE,{"disambiguationData":[OSD([sQuery(id+"F5.wireOp",EDGE,"E19.2.0.0"),sQuery(id+"F5.wireOp",EDGE,"E19.2.0.1")])],"isStart":true}),makeQuery(id+"F6.opExtrude","CAP_FACE",FACE,{"disambiguationData":[OSD([sQuery(id+"F5.wireOp",EDGE,"E19.3.0.0"),sQuery(id+"F5.wireOp",EDGE,"E19.3.0.1")])],"isStart":true}),makeQuery(id+"F6.opExtrude","CAP_FACE",FACE,{"disambiguationData":[OSD([sQuery(id+"F5.wireOp",EDGE,"E19.4.0.0"),sQuery(id+"F5.wireOp",EDGE,"E19.4.0.1")])],"isStart":true}),makeQuery(id+"F6.opExtrude","CAP_FACE",FACE,{"disambiguationData":[OSD([sQuery(id+"F5.wireOp",EDGE,"E19.5.0.0"),sQuery(id+"F5.wireOp",EDGE,"E19.5.0.1")])],"isStart":true}),makeQuery(id+"F6.opExtrude","CAP_FACE",FACE,{"disambiguationData":[OSD([sQuery(id+"F5.wireOp",EDGE,"E19.6.0.0"),sQuery(id+"F5.wireOp",EDGE,"E19.6.0.1")])],"isStart":true}),makeQuery(id+"F6.opExtrude","CAP_FACE",FACE,{"disambiguationData":[OSD([sQuery(id+"F5.wireOp",EDGE,"E19.7.0.0"),sQuery(id+"F5.wireOp",EDGE,"E19.7.0.1")])],"isStart":true}),makeQuery(id+"F6.opExtrude","CAP_FACE",FACE,{"disambiguationData":[OSD([sQuery(id+"F5.wireOp",EDGE,"E19.8.0.0"),sQuery(id+"F5.wireOp",EDGE,"E19.8.0.1")])],"isStart":true}),makeQuery(id+"F6.opExtrude","CAP_FACE",FACE,{"disambiguationData":[OSD([sQuery(id+"F5.wireOp",EDGE,"E19.9.0.0"),sQuery(id+"F5.wireOp",EDGE,"E19.9.0.1")])],"isStart":true})])],"derivedFrom":subQ6});}
            var sketch = newSketch(context, id + "F17", { "sketchPlane" : qUnion([Q0])});
            skCircle(sketch, "E31", {"center": v(23.57, 60) * mm, "radius": 5 * mm});
            skCircle(sketch, "E32", {"center": v(-23.57, 60) * mm, "radius": 5 * mm});
            skCircle(sketch, "E33", {"center": v(-23.57, 15) * mm, "radius": 5 * mm});
            skCircle(sketch, "E34", {"center": v(23.57, 15) * mm, "radius": 5 * mm});
            skCircle(sketch, "E35", {"center": v(6, 10) * mm, "radius": 5 * mm});
            skCircle(sketch, "E36", {"center": v(-6, 10) * mm, "radius": 5 * mm});
            skSolve(sketch);
        }
        {
            var Q0;
            Q0 = qSketchRegion(id + "F17", true);
            extrude(context, id + "F18", {"entities" : qUnion([Q0]), "operationType" : NewBodyOperationType.REMOVE, "depth" : 25 * mm});
        }
        {
            var Q0;
            Q0=makeQuery(id+"F2.opExtrude","CAP_FACE",FACE,{"disambiguationData":[OSD([sQuery(id+"F1.wireOp",EDGE,"E0"),sQuery(id+"F1.wireOp",EDGE,"E1"),sQuery(id+"F1.wireOp",EDGE,"E2"),sQuery(id+"F1.wireOp",EDGE,"E3.MirrorCS"),sQuery(id+"F1.wireOp",EDGE,"E4.MirrorCS"),sQuery(id+"F1.wireOp",EDGE,"E5.MirrorCS")])],"isStart":true});
            var sketch = newSketch(context, id + "F19", { "sketchPlane" : qUnion([Q0])});
            skLineSegment(sketch, "E37.left", {"start": v(15.57, 23.08) * mm, "end": v(15.57, 128.43) * mm});
            skLineSegment(sketch, "E37.right", {"start": v(-15.57, 23.08) * mm, "end": v(-15.57, 128.43) * mm});
            skPoint(sketch, "E38", {"position": v(23.57, 15) * mm});
            skPoint(sketch, "E39", {"position": v(-23.57, 15) * mm});
            skArc(sketch, "E40", {"start": v(15.57, 128.43) * mm, "mid": v(0, 130) * mm, "end": v(-15.57, 128.43) * mm});
            skArc(sketch, "E41", {"start": v(60, 0) * mm, "mid": v(56.93, 62.32) * mm, "end": v(31.57, 119.34) * mm});
            skLineSegment(sketch, "E42", {"start": v(60, 0) * mm, "end": v(31.57, 0) * mm});
            skLineSegment(sketch, "E43", {"start": v(31.57, 0) * mm, "end": v(31.57, 119.34) * mm});
            skLineSegment(sketch, "E44.MirrorCS", {"start": v(-60, 0) * mm, "end": v(-31.57, 0) * mm});
            skArc(sketch, "E45.MirrorCS", {"start": v(-60, 0) * mm, "mid": v(-56.93, 62.32) * mm, "end": v(-31.57, 119.34) * mm});
            skLineSegment(sketch, "E46.MirrorCS", {"start": v(-31.57, 0) * mm, "end": v(-31.57, 119.34) * mm});
            skLineSegment(sketch, "E47", {"start": v(-15.57, 23.08) * mm, "end": v(15.57, 23.08) * mm});
            skPoint(sketch, "E48", {"position": v(0, 23.08) * mm});
            skSolve(sketch);
        }
        {
            var Q0;
            Q0 = qSketchRegion(id + "F19", true);
            extrude(context, id + "F20", {"entities" : qUnion([Q0]), "operationType" : NewBodyOperationType.ADD, "depth" : 3 * mm});
        }
        {
            var Q0;
            Q0=makeQuery(id+"F20.opExtrude","CAP_EDGE",EDGE,{"disambiguationData":[OSD([sQuery(id+"F19.wireOp",EDGE,"E37.left")])],"isStart":false});
            var Q1;
            Q1=makeQuery(id+"F20.opExtrude","CAP_EDGE",EDGE,{"disambiguationData":[OSD([sQuery(id+"F19.wireOp",EDGE,"E37.right")])],"isStart":false});
            var Q2;
            Q2=makeQuery(id+"F20.opExtrude","CAP_EDGE",EDGE,{"disambiguationData":[OSD([sQuery(id+"F19.wireOp",EDGE,"E46.MirrorCS")])],"isStart":false});
            var Q3;
            Q3=makeQuery(id+"F20.opExtrude","CAP_EDGE",EDGE,{"disambiguationData":[OSD([sQuery(id+"F19.wireOp",EDGE,"E43")])],"isStart":false});
            var Q4;
            Q4=makeQuery(id+"F20.opExtrude","CAP_EDGE",EDGE,{"disambiguationData":[OSD([sQuery(id+"F19.wireOp",EDGE,"zS66gYXZ-0WJ1-GNRd-CW5H-YCuno0UtB482")])],"isStart":false});
            var Q5;
            Q5=makeQuery(id+"F20.opExtrude","CAP_EDGE",EDGE,{"disambiguationData":[OSD([sQuery(id+"F19.wireOp",EDGE,"E47")])],"isStart":false});
            var Q6;
            Q6=makeQuery(id+"F20.opExtrude","CAP_EDGE",EDGE,{"disambiguationData":[OSD([sQuery(id+"F19.wireOp",EDGE,"6rLx0d4R-H4u5-pnFk-er2m-jyyjp0cNVsxB")])],"isStart":false});
            chamfer(context, id + "F21", {"entities" : qUnion([Q0, Q1, Q2, Q3, Q4, Q5, Q6]), "width" : 3 * mm, "tangentPropagation" : true});
        }
        {
            var Q0;
            Q0=makeQuery(id+"F4.opExtrude","CAP_FACE",FACE,{"disambiguationData":[OSD([sQuery(id+"F3.wireOp",EDGE,"E6"),sQuery(id+"F3.wireOp",EDGE,"E7"),sQuery(id+"F3.wireOp",EDGE,"E8"),sQuery(id+"F3.wireOp",EDGE,"E9"),sQuery(id+"F3.wireOp",EDGE,"E10"),sQuery(id+"F3.wireOp",EDGE,"E11"),sQuery(id+"F3.wireOp",EDGE,"E12"),sQuery(id+"F3.wireOp",EDGE,"E13")])],"isStart":false});
            var sketch = newSketch(context, id + "F22", { "sketchPlane" : qUnion([Q0])});
            skArc(sketch, "E49", {"start": v(27.5, 125) * mm, "mid": v(0, 130) * mm, "end": v(-27.5, 125) * mm});
            skArc(sketch, "E50", {"start": v(-27.5, 125) * mm, "mid": v(-36.27, 112.13) * mm, "end": v(-43.83, 98.51) * mm});
            skArc(sketch, "E51", {"start": v(43.83, 98.51) * mm, "mid": v(36.27, 112.13) * mm, "end": v(27.5, 125) * mm});
            skPoint(sketch, "E52", {"position": v(0, 114.28) * mm});
            skArc(sketch, "E53", {"start": v(32.68, 98.51) * mm, "mid": v(0, 109.28) * mm, "end": v(-32.68, 98.51) * mm});
            skPoint(sketch, "E54", {"position": v(0, 109.28) * mm});
            skArc(sketch, "E55", {"start": v(-43.83, 98.51) * mm, "mid": v(-47.29, 91.1) * mm, "end": v(-50.4, 83.51) * mm});
            skLineSegment(sketch, "E56", {"start": v(-50.4, 83.51) * mm, "end": v(-39.74, 83.51) * mm});
            skArc(sketch, "E57", {"start": v(-32.68, 98.51) * mm, "mid": v(-36.4, 91.1) * mm, "end": v(-39.74, 83.51) * mm});
            skArc(sketch, "E58.MirrorCS", {"start": v(32.68, 98.51) * mm, "mid": v(36.4, 91.1) * mm, "end": v(39.74, 83.51) * mm});
            skArc(sketch, "E59.MirrorCS", {"start": v(43.83, 98.51) * mm, "mid": v(47.29, 91.1) * mm, "end": v(50.4, 83.51) * mm});
            skLineSegment(sketch, "E60.MirrorCS", {"start": v(50.4, 83.51) * mm, "end": v(39.74, 83.51) * mm});
            skSolve(sketch);
        }
        {
            var Q0;
            Q0 = qSketchRegion(id + "F22", true);
            extrude(context, id + "F23", {"entities" : qUnion([Q0]), "operationType" : NewBodyOperationType.ADD, "depth" : 5 * mm});
        }
        {
            var Q0;
            Q0=qCreatedBy(makeId("Right.planeOp"),FACE);
            var sketch = newSketch(context, id + "F24", { "sketchPlane" : qUnion([Q0])});
            skLineSegment(sketch, "E61", {"start": v(-19.65, 91.35) * mm, "end": v(-21.35, 94.68) * mm});
            skLineSegment(sketch, "E62", {"start": v(-23, 101.51) * mm, "end": v(-23, 105.4) * mm});
            skLineSegment(sketch, "E63", {"start": v(-23, 105.4) * mm, "end": v(-29.66, 105.4) * mm});
            skLineSegment(sketch, "E64", {"start": v(-29.66, 105.4) * mm, "end": v(-29.66, 83.51) * mm});
            skLineSegment(sketch, "E65", {"start": v(-29.66, 83.51) * mm, "end": v(-18, 83.51) * mm});
            skLineSegment(sketch, "E66", {"start": v(-18, 83.51) * mm, "end": v(-18, 84.51) * mm});
            skPoint(sketch, "E67.visualSharp", {"position": v(-18, 88.13) * mm});
            skArc(sketch, "E67.filletArc", {"start": v(-18, 84.51) * mm, "mid": v(-18.42, 88.03) * mm, "end": v(-19.65, 91.35) * mm});
            skPoint(sketch, "E68.visualSharp", {"position": v(-23, 97.9) * mm});
            skArc(sketch, "E68.filletArc", {"start": v(-23, 101.51) * mm, "mid": v(-22.58, 98) * mm, "end": v(-21.35, 94.68) * mm});
            skSolve(sketch);
        }
        {
            var Q0;
            Q0 = qSketchRegion(id + "F24", true);
            extrude(context, id + "F25", {"entities" : qUnion([Q0]), "operationType" : NewBodyOperationType.REMOVE, "endBound" : BoundingType.THROUGH_ALL, "oppositeDirection" : true, "depth" : 25 * mm, "hasSecondDirection" : true, "secondDirectionBound" : SecondDirectionBoundingType.THROUGH_ALL, "secondDirectionOppositeDirection" : false, "secondDirectionDepth" : 25 * mm});
        }
        {
            var Q0;
            Q0=makeQuery(id+"F23.opExtrude","SWEPT_EDGE",EDGE,{"disambiguationData":[OSD([sQuery(id+"F3.wireOp",EDGE,"E10"),sQuery(id+"F22.wireOp",EDGE,"E53"),sQuery(id+"F22.wireOp",EDGE,"E57")])]});
            var Q1;
            Q1=makeQuery(id+"F23.opExtrude","SWEPT_EDGE",EDGE,{"disambiguationData":[OSD([sQuery(id+"F3.wireOp",EDGE,"E11"),sQuery(id+"F22.wireOp",EDGE,"E53"),sQuery(id+"F22.wireOp",EDGE,"E58.MirrorCS")])]});
            fillet(context, id + "F26", {"entities" : qUnion([Q0, Q1]), "radius" : 10 * mm, "tangentPropagation" : true, "allowEdgeOverflow" : false});
        }
        {
            var Q0;
            Q0=makeQuery(id+"F4.opExtrude","SWEPT_FACE",FACE,{"disambiguationData":[OSD([sQuery(id+"F3.wireOp",EDGE,"E14")])]});
            var sketch = newSketch(context, id + "F27", { "sketchPlane" : qUnion([Q0])});
            skCircle(sketch, "E69", {"center": v(-10.5, 11.46) * mm, "radius": 2.5 * mm});
            skCircle(sketch, "E70", {"center": v(-10.5, 34.4) * mm, "radius": 2.5 * mm});
            skLineSegment(sketch, "E71", {"start": v(-18, 0) * mm, "end": v(-18, 22.93) * mm});
            skLineSegment(sketch, "E72", {"start": v(-18, 22.93) * mm, "end": v(-18, 45.86) * mm});
            skPoint(sketch, "E73", {"position": v(-18, 11.46) * mm});
            skPoint(sketch, "E74", {"position": v(-18, 34.4) * mm});
            skSolve(sketch);
        }
        {
            var Q0;
            Q0 = qSketchRegion(id + "F27", true);
            extrude(context, id + "F28", {"entities" : qUnion([Q0]), "operationType" : NewBodyOperationType.REMOVE, "oppositeDirection" : true, "depth" : 25 * mm, "hasSecondDirection" : true, "secondDirectionBound" : SecondDirectionBoundingType.THROUGH_ALL, "secondDirectionOppositeDirection" : false, "secondDirectionDepth" : 25 * mm});
        }
        {
            var Q0;
            Q0=makeQuery(id+"F4.opExtrude","SWEPT_FACE",FACE,{"disambiguationData":[OSD([sQuery(id+"F3.wireOp",EDGE,"E14")])]});
            var sketch = newSketch(context, id + "F29", { "sketchPlane" : qUnion([Q0])});
            skCircle(sketch, "E75.cCircle", {"center": v(-10.5, 11.46) * mm, "radius": 4.03 * mm, "construction": true});
            skLineSegment(sketch, "E75.0", {"start": v(-14.53, 13.79) * mm, "end": v(-10.5, 16.11) * mm});
            skLineSegment(sketch, "E75.1", {"start": v(-10.5, 16.11) * mm, "end": v(-6.48, 13.79) * mm});
            skLineSegment(sketch, "E75.2", {"start": v(-6.47, 13.79) * mm, "end": v(-6.47, 9.14) * mm});
            skLineSegment(sketch, "E75.3", {"start": v(-6.47, 9.14) * mm, "end": v(-10.5, 6.82) * mm});
            skLineSegment(sketch, "E75.4", {"start": v(-10.5, 6.82) * mm, "end": v(-14.52, 9.14) * mm});
            skLineSegment(sketch, "E75.5", {"start": v(-14.53, 9.14) * mm, "end": v(-14.53, 13.79) * mm});
            skPoint(sketch, "E75.0.midPoint", {"position": v(-12.51, 14.95) * mm});
            skCircle(sketch, "E76.cCircle", {"center": v(-10.5, 34.4) * mm, "radius": 4.03 * mm, "construction": true});
            skLineSegment(sketch, "E76.0", {"start": v(-14.53, 36.72) * mm, "end": v(-10.5, 39.04) * mm});
            skLineSegment(sketch, "E76.1", {"start": v(-10.5, 39.04) * mm, "end": v(-6.47, 36.72) * mm});
            skLineSegment(sketch, "E76.2", {"start": v(-6.48, 36.72) * mm, "end": v(-6.48, 32.07) * mm});
            skLineSegment(sketch, "E76.3", {"start": v(-6.47, 32.07) * mm, "end": v(-10.5, 29.75) * mm});
            skLineSegment(sketch, "E76.4", {"start": v(-10.5, 29.75) * mm, "end": v(-14.52, 32.07) * mm});
            skLineSegment(sketch, "E76.5", {"start": v(-14.53, 32.07) * mm, "end": v(-14.53, 36.72) * mm});
            skPoint(sketch, "E76.0.midPoint", {"position": v(-12.51, 37.88) * mm});
            skSolve(sketch);
        }
        {
            var Q0;
            Q0 = qSketchRegion(id + "F29", true);
            extrude(context, id + "F30", {"entities" : qUnion([Q0]), "operationType" : NewBodyOperationType.REMOVE, "oppositeDirection" : true, "depth" : 4 * mm});
        }
        {
            var Q0;
            Q0=makeQuery(id+"F4.opExtrude","SWEPT_FACE",FACE,{"disambiguationData":[OSD([sQuery(id+"F3.wireOp",EDGE,"E16.MirrorCS")])]});
            var sketch = newSketch(context, id + "F31", { "sketchPlane" : qUnion([Q0])});
            skCircle(sketch, "E77.cCircle", {"center": v(10.5, 34.4) * mm, "radius": 4.03 * mm, "construction": true});
            skLineSegment(sketch, "E77.0", {"start": v(14.52, 36.72) * mm, "end": v(14.52, 32.07) * mm});
            skLineSegment(sketch, "E77.1", {"start": v(14.53, 32.07) * mm, "end": v(10.5, 29.75) * mm});
            skLineSegment(sketch, "E77.2", {"start": v(10.5, 29.75) * mm, "end": v(6.48, 32.07) * mm});
            skLineSegment(sketch, "E77.3", {"start": v(6.47, 32.07) * mm, "end": v(6.47, 36.72) * mm});
            skLineSegment(sketch, "E77.4", {"start": v(6.48, 36.72) * mm, "end": v(10.5, 39.04) * mm});
            skLineSegment(sketch, "E77.5", {"start": v(10.5, 39.04) * mm, "end": v(14.53, 36.72) * mm});
            skPoint(sketch, "E77.0.midPoint", {"position": v(14.53, 34.4) * mm});
            skCircle(sketch, "E78.cCircle", {"center": v(10.5, 11.46) * mm, "radius": 4.03 * mm, "construction": true});
            skLineSegment(sketch, "E78.0", {"start": v(14.53, 13.79) * mm, "end": v(14.53, 9.14) * mm});
            skLineSegment(sketch, "E78.1", {"start": v(14.53, 9.14) * mm, "end": v(10.5, 6.82) * mm});
            skLineSegment(sketch, "E78.2", {"start": v(10.5, 6.82) * mm, "end": v(6.47, 9.14) * mm});
            skLineSegment(sketch, "E78.3", {"start": v(6.47, 9.14) * mm, "end": v(6.47, 13.79) * mm});
            skLineSegment(sketch, "E78.4", {"start": v(6.47, 13.79) * mm, "end": v(10.5, 16.11) * mm});
            skLineSegment(sketch, "E78.5", {"start": v(10.5, 16.11) * mm, "end": v(14.53, 13.79) * mm});
            skPoint(sketch, "E78.0.midPoint", {"position": v(14.53, 11.46) * mm});
            skSolve(sketch);
        }
        {
            var Q0;
            Q0 = qSketchRegion(id + "F31", true);
            extrude(context, id + "F32", {"entities" : qUnion([Q0]), "operationType" : NewBodyOperationType.REMOVE, "oppositeDirection" : true, "depth" : 4 * mm});
        }
        {
            var Q0;
            Q0=makeQuery(id+"F4.opExtrude","SWEPT_FACE",FACE,{"disambiguationData":[OSD([sQuery(id+"F3.wireOp",EDGE,"E14")])]});
            cPlane(context, id + "F33", {"entities" : qUnion([Q0]), "cplaneType" : CPlaneType.OFFSET, "offset" : (getVariable(context, 'TWall') - 2) * mm, "oppositeDirection" : true, "width" : 150 * mm, "height" : 150 * mm});
        }
        {
            var Q0;
            Q0=qCreatedBy(id+"F33.planeOp",FACE);
            var sketch = newSketch(context, id + "F34", { "sketchPlane" : qUnion([Q0])});
            skCircle(sketch, "E79", {"center": v(-10.5, 11.46) * mm, "radius": 5 * mm});
            skCircle(sketch, "E80", {"center": v(-10.5, 34.4) * mm, "radius": 5 * mm});
            skSolve(sketch);
        }
        {
            var Q0;
            Q0 = qSketchRegion(id + "F34", true);
            extrude(context, id + "F35", {"entities" : qUnion([Q0]), "operationType" : NewBodyOperationType.REMOVE, "oppositeDirection" : true, "depth" : 25 * mm});
        }
        {
            var Q0;
            Q0=makeQuery(id+"F4.opExtrude","SWEPT_FACE",FACE,{"disambiguationData":[OSD([sQuery(id+"F3.wireOp",EDGE,"E16.MirrorCS")])]});
            cPlane(context, id + "F36", {"entities" : qUnion([Q0]), "cplaneType" : CPlaneType.OFFSET, "offset" : 8 * mm, "oppositeDirection" : true, "width" : 150 * mm, "height" : 150 * mm});
        }
        {
            var Q0;
            Q0=qCreatedBy(id+"F36.planeOp",FACE);
            var sketch = newSketch(context, id + "F37", { "sketchPlane" : qUnion([Q0])});
            skCircle(sketch, "E81", {"center": v(10.5, 34.4) * mm, "radius": 5 * mm});
            skCircle(sketch, "E82", {"center": v(10.5, 11.46) * mm, "radius": 5 * mm});
            skSolve(sketch);
        }
        {
            var Q0;
            Q0 = qSketchRegion(id + "F37", true);
            extrude(context, id + "F38", {"entities" : qUnion([Q0]), "operationType" : NewBodyOperationType.REMOVE, "oppositeDirection" : true, "depth" : 25 * mm});
        }
    });
